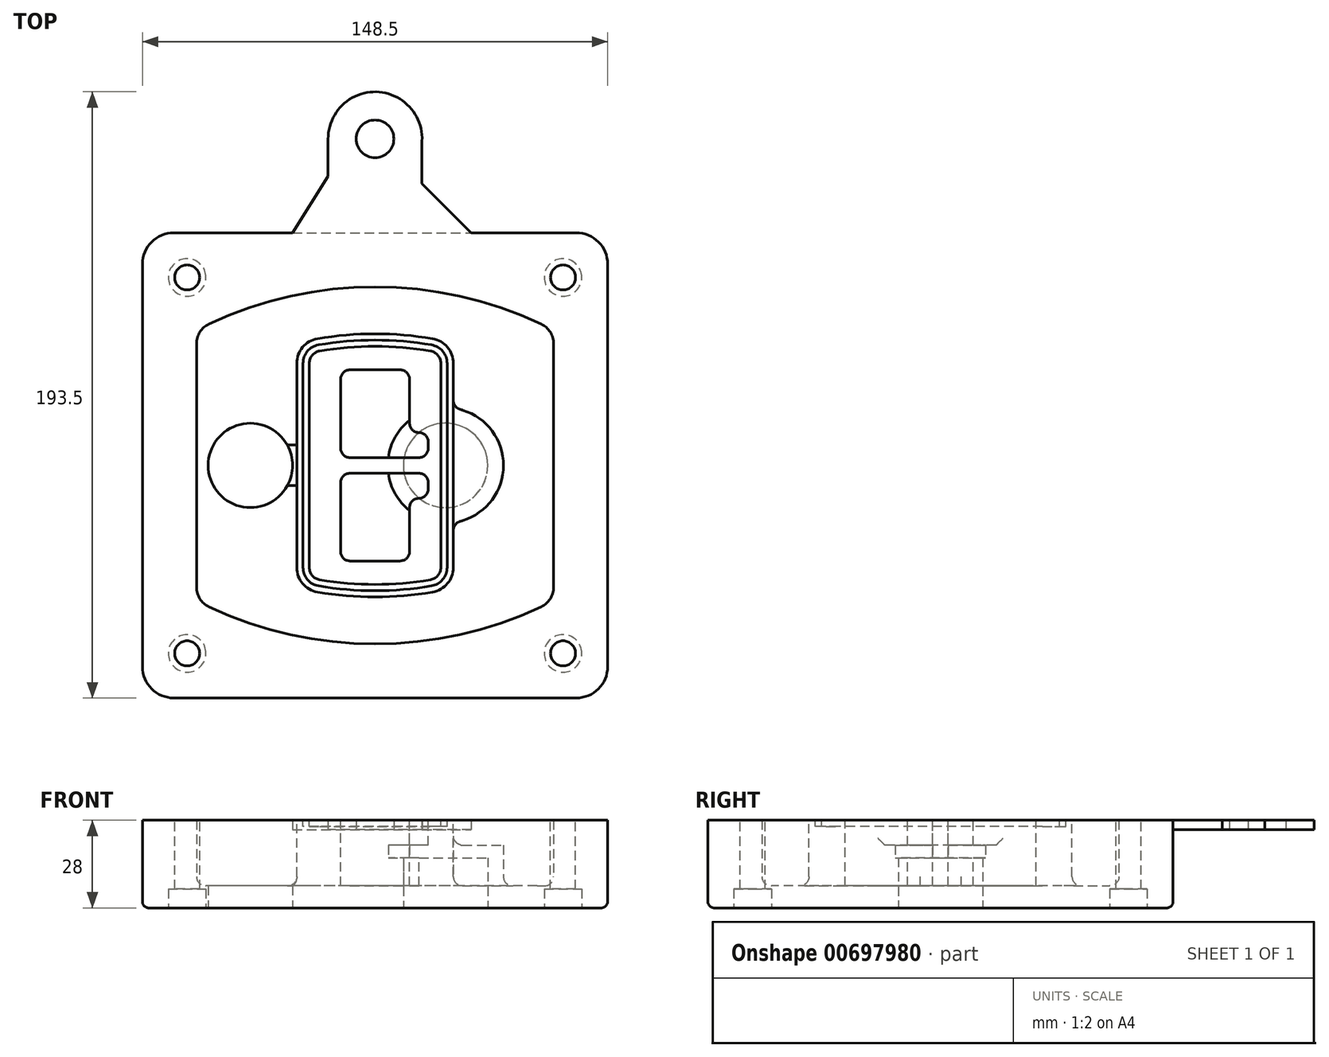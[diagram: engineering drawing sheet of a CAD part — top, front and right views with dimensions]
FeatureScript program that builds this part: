
annotation { "Feature Type Name" : "Feature", "Feature Type Description" : "" }
export const myFeature = defineFeature(function(context is Context, id is Id, definition is map)
    precondition{}
    {
        {
            var Q0;
            Q0=qCreatedBy(makeId("Top.planeOp"),FACE);
            var sketch = newSketch(context, id + "F0", { "sketchPlane" : qUnion([Q0])});
            skPoint(sketch, "E0.rect.middle", {"position": v(0, 0) * mm});
            skLineSegment(sketch, "E1.bottom", {"start": v(-64.25, -74.25) * mm, "end": v(64.25, -74.25) * mm});
            skLineSegment(sketch, "E1.top", {"start": v(-64.25, 74.25) * mm, "end": v(64.25, 74.25) * mm});
            skLineSegment(sketch, "E1.left", {"start": v(-74.25, -64.25) * mm, "end": v(-74.25, 64.25) * mm});
            skLineSegment(sketch, "E1.right", {"start": v(74.25, -64.25) * mm, "end": v(74.25, 64.25) * mm});
            skLineSegment(sketch, "E2", {"start": v(-74.25, 74.25) * mm, "end": v(74.25, -74.25) * mm, "construction": true});
            skLineSegment(sketch, "E3", {"start": v(74.25, 74.25) * mm, "end": v(-74.25, -74.25) * mm, "construction": true});
            skCircle(sketch, "E4", {"center": v(-60, 60) * mm, "radius": 4 * mm});
            skCircle(sketch, "E5", {"center": v(60, 60) * mm, "radius": 4 * mm});
            skCircle(sketch, "E6", {"center": v(60, -60) * mm, "radius": 4 * mm});
            skCircle(sketch, "E7", {"center": v(-60, -60) * mm, "radius": 4 * mm});
            skLineSegment(sketch, "E8", {"start": v(-60, 60) * mm, "end": v(60, 60) * mm, "construction": true});
            skLineSegment(sketch, "E9", {"start": v(60, 60) * mm, "end": v(60, -60) * mm, "construction": true});
            skLineSegment(sketch, "E10", {"start": v(60, -60) * mm, "end": v(-60, -60) * mm, "construction": true});
            skLineSegment(sketch, "E11", {"start": v(-60, -60) * mm, "end": v(-60, 60) * mm, "construction": true});
            skLineSegment(sketch, "E12", {"start": v(-60, 38.83) * mm, "end": v(-60, -38.83) * mm});
            skLineSegment(sketch, "E13", {"start": v(60, 38.83) * mm, "end": v(60, -38.83) * mm});
            skArc(sketch, "E14", {"start": v(54.26, 47.88) * mm, "mid": v(0, 60) * mm, "end": v(-54.26, 47.88) * mm});
            skArc(sketch, "E15", {"start": v(-54.26, -47.88) * mm, "mid": v(0, -60) * mm, "end": v(54.26, -47.88) * mm});
            skLineSegment(sketch, "E16", {"start": v(-60, 0) * mm, "end": v(60, 0) * mm, "construction": true});
            skPoint(sketch, "E17.visualSharp", {"position": v(-60, -45) * mm});
            skArc(sketch, "E17.filletArc", {"start": v(-60, -38.83) * mm, "mid": v(-58.44, -44.2) * mm, "end": v(-54.26, -47.88) * mm});
            skPoint(sketch, "E18.visualSharp", {"position": v(-60, 45) * mm});
            skArc(sketch, "E18.filletArc", {"start": v(-54.26, 47.88) * mm, "mid": v(-58.44, 44.2) * mm, "end": v(-60, 38.83) * mm});
            skPoint(sketch, "E19.visualSharp", {"position": v(60, 45) * mm});
            skArc(sketch, "E19.filletArc", {"start": v(60, 38.83) * mm, "mid": v(58.44, 44.2) * mm, "end": v(54.26, 47.88) * mm});
            skPoint(sketch, "E20.visualSharp", {"position": v(60, -45) * mm});
            skArc(sketch, "E20.filletArc", {"start": v(54.26, -47.88) * mm, "mid": v(58.44, -44.2) * mm, "end": v(60, -38.83) * mm});
            skPoint(sketch, "E21.visualSharp", {"position": v(-74.25, 74.25) * mm});
            skArc(sketch, "E21.filletArc", {"start": v(-64.25, 74.25) * mm, "mid": v(-71.32, 71.32) * mm, "end": v(-74.25, 64.25) * mm});
            skPoint(sketch, "E22.visualSharp", {"position": v(74.25, 74.25) * mm});
            skArc(sketch, "E22.filletArc", {"start": v(74.25, 64.25) * mm, "mid": v(71.32, 71.32) * mm, "end": v(64.25, 74.25) * mm});
            skPoint(sketch, "E23.visualSharp", {"position": v(74.25, -74.25) * mm});
            skArc(sketch, "E23.filletArc", {"start": v(64.25, -74.25) * mm, "mid": v(71.32, -71.32) * mm, "end": v(74.25, -64.25) * mm});
            skPoint(sketch, "E24.visualSharp", {"position": v(-74.25, -74.25) * mm});
            skArc(sketch, "E24.filletArc", {"start": v(-74.25, -64.25) * mm, "mid": v(-71.32, -71.32) * mm, "end": v(-64.25, -74.25) * mm});
            skArc(sketch, "E25.0", {"start": v(57, 38.83) * mm, "mid": v(55.9, 42.58) * mm, "end": v(52.98, 45.17) * mm});
            skLineSegment(sketch, "E25.1", {"start": v(57, 38.83) * mm, "end": v(57, -38.83) * mm});
            skArc(sketch, "E25.2", {"start": v(52.98, -45.17) * mm, "mid": v(55.9, -42.58) * mm, "end": v(57, -38.83) * mm});
            skArc(sketch, "E25.3", {"start": v(-52.98, -45.17) * mm, "mid": v(0, -57) * mm, "end": v(52.98, -45.17) * mm});
            skArc(sketch, "E25.4", {"start": v(-57, -38.83) * mm, "mid": v(-55.9, -42.58) * mm, "end": v(-52.98, -45.17) * mm});
            skArc(sketch, "E25.5", {"start": v(52.98, 45.17) * mm, "mid": v(0, 57) * mm, "end": v(-52.98, 45.17) * mm});
            skLineSegment(sketch, "E25.6", {"start": v(-57, 38.83) * mm, "end": v(-57, -38.83) * mm});
            skArc(sketch, "E25.7", {"start": v(-52.98, 45.17) * mm, "mid": v(-55.9, 42.58) * mm, "end": v(-57, 38.83) * mm});
            skArc(sketch, "E26.0", {"start": v(-55.96, 51.5) * mm, "mid": v(-61.82, 46.33) * mm, "end": v(-64, 38.83) * mm});
            skArc(sketch, "E26.1", {"start": v(55.96, 51.5) * mm, "mid": v(0, 64) * mm, "end": v(-55.96, 51.5) * mm});
            skArc(sketch, "E26.2", {"start": v(64, 38.83) * mm, "mid": v(61.82, 46.33) * mm, "end": v(55.96, 51.5) * mm});
            skLineSegment(sketch, "E26.3", {"start": v(64, 38.83) * mm, "end": v(64, -38.83) * mm});
            skArc(sketch, "E26.4", {"start": v(55.96, -51.5) * mm, "mid": v(61.82, -46.33) * mm, "end": v(64, -38.83) * mm});
            skLineSegment(sketch, "E26.5", {"start": v(-64, 38.83) * mm, "end": v(-64, -38.83) * mm});
            skArc(sketch, "E26.6", {"start": v(-55.96, -51.5) * mm, "mid": v(0, -64) * mm, "end": v(55.96, -51.5) * mm});
            skArc(sketch, "E26.7", {"start": v(-64, -38.83) * mm, "mid": v(-61.82, -46.33) * mm, "end": v(-55.96, -51.5) * mm});
            skSolve(sketch);
        }
        {
            var Q0;
            Q0=makeQuery(id+"F0.imprint","IMPRINT",FACE,{"disambiguationData":[TD([[makeQuery(id+"F0.imprint","IMPRINT",EDGE,{"derivedFrom":sQuery(id+"F0.wireOp",EDGE,"E1.bottom")}),1.0]])]});
            var Q1;
            Q1=makeQuery(id+"F0.imprint","IMPRINT",FACE,{"disambiguationData":[TD([[makeQuery(id+"F0.imprint","IMPRINT",EDGE,{"derivedFrom":sQuery(id+"F0.wireOp",EDGE,"E12")}),1.0]])]});
            var Q2;
            Q2=makeQuery(id+"F0.imprint","IMPRINT",FACE,{"disambiguationData":[TD([[makeQuery(id+"F0.imprint","IMPRINT",EDGE,{"derivedFrom":sQuery(id+"F0.wireOp",EDGE,"E25.0")}),1.0]])]});
            var Q3;
            Q3=makeQuery(id+"F0.imprint","IMPRINT",FACE,{"disambiguationData":[TD([[makeQuery(id+"F0.imprint","IMPRINT",EDGE,{"derivedFrom":sQuery(id+"F0.wireOp",EDGE,"E12")}),-1.0]])]});
            extrude(context, id + "F1", {"entities" : qUnion([Q0, Q1, Q2, Q3]), "oppositeDirection" : true, "depth" : 25 * mm});
        }
        {
            var Q0;
            Q0=makeQuery(id+"F0.imprint","IMPRINT",FACE,{"disambiguationData":[TD([[makeQuery(id+"F0.imprint","IMPRINT",EDGE,{"derivedFrom":sQuery(id+"F0.wireOp",EDGE,"E12")}),1.0]])]});
            extrude(context, id + "F2", {"entities" : qUnion([Q0]), "operationType" : NewBodyOperationType.ADD, "depth" : 3 * mm});
        }
        {
            var Q0;
            Q0=makeQuery(id+"F0.imprint","IMPRINT",FACE,{"disambiguationData":[TD([[makeQuery(id+"F0.imprint","IMPRINT",EDGE,{"derivedFrom":sQuery(id+"F0.wireOp",EDGE,"E25.0")}),1.0]])]});
            extrude(context, id + "F3", {"entities" : qUnion([Q0]), "operationType" : NewBodyOperationType.REMOVE, "oppositeDirection" : true, "depth" : 18 * mm});
        }
        {
            var Q0;
            Q0=makeQuery(id+"F2.opExtrude","CAP_FACE",FACE,{"disambiguationData":[OSD([sQuery(id+"F0.wireOp",EDGE,"E12"),sQuery(id+"F0.wireOp",EDGE,"E13"),sQuery(id+"F0.wireOp",EDGE,"E14"),sQuery(id+"F0.wireOp",EDGE,"E15"),sQuery(id+"F0.wireOp",EDGE,"E17.filletArc"),sQuery(id+"F0.wireOp",EDGE,"E18.filletArc"),sQuery(id+"F0.wireOp",EDGE,"E19.filletArc"),sQuery(id+"F0.wireOp",EDGE,"E20.filletArc"),sQuery(id+"F0.wireOp",EDGE,"E25.0"),sQuery(id+"F0.wireOp",EDGE,"E25.1"),sQuery(id+"F0.wireOp",EDGE,"E25.2"),sQuery(id+"F0.wireOp",EDGE,"E25.3"),sQuery(id+"F0.wireOp",EDGE,"E25.4"),sQuery(id+"F0.wireOp",EDGE,"E25.5"),sQuery(id+"F0.wireOp",EDGE,"E25.6"),sQuery(id+"F0.wireOp",EDGE,"E25.7")])],"isStart":false});
            var sketch = newSketch(context, id + "F4", { "sketchPlane" : qUnion([Q0])});
            skArc(sketch, "E27.0", {"start": v(-18.34, -40.45) * mm, "mid": v(0, -42) * mm, "end": v(18.34, -40.45) * mm});
            skArc(sketch, "E28.0", {"start": v(18.34, 40.45) * mm, "mid": v(0, 42) * mm, "end": v(-18.34, 40.45) * mm});
            skLineSegment(sketch, "E29", {"start": v(-25, 32.57) * mm, "end": v(-25, -32.57) * mm});
            skLineSegment(sketch, "E30", {"start": v(25, 32.57) * mm, "end": v(25, -32.57) * mm});
            skLineSegment(sketch, "E31", {"start": v(-25, 39.1) * mm, "end": v(25, 39.1) * mm, "construction": true});
            skLineSegment(sketch, "E32", {"start": v(-25, -39.1) * mm, "end": v(25, -39.1) * mm, "construction": true});
            skPoint(sketch, "E33.visualSharp", {"position": v(-25, 39.1) * mm});
            skArc(sketch, "E33.filletArc", {"start": v(-18.34, 40.45) * mm, "mid": v(-23.11, 37.73) * mm, "end": v(-25, 32.57) * mm});
            skPoint(sketch, "E34.visualSharp", {"position": v(25, 39.1) * mm});
            skArc(sketch, "E34.filletArc", {"start": v(25, 32.57) * mm, "mid": v(23.11, 37.73) * mm, "end": v(18.34, 40.45) * mm});
            skPoint(sketch, "E35.visualSharp", {"position": v(25, -39.1) * mm});
            skArc(sketch, "E35.filletArc", {"start": v(18.34, -40.45) * mm, "mid": v(23.11, -37.73) * mm, "end": v(25, -32.57) * mm});
            skPoint(sketch, "E36.visualSharp", {"position": v(-25, -39.1) * mm});
            skArc(sketch, "E36.filletArc", {"start": v(-25, -32.57) * mm, "mid": v(-23.11, -37.73) * mm, "end": v(-18.34, -40.45) * mm});
            skArc(sketch, "E37.0", {"start": v(52.98, 45.17) * mm, "mid": v(0, 57) * mm, "end": v(-52.98, 45.17) * mm});
            skArc(sketch, "E37.1", {"start": v(-52.98, 45.17) * mm, "mid": v(-55.9, 42.58) * mm, "end": v(-57, 38.83) * mm});
            skLineSegment(sketch, "E37.2", {"start": v(-57, 38.83) * mm, "end": v(-57, -38.83) * mm});
            skArc(sketch, "E37.3", {"start": v(-57, -38.83) * mm, "mid": v(-55.9, -42.58) * mm, "end": v(-52.98, -45.17) * mm});
            skArc(sketch, "E37.4", {"start": v(-52.98, -45.17) * mm, "mid": v(0, -57) * mm, "end": v(52.98, -45.17) * mm});
            skArc(sketch, "E37.5", {"start": v(52.98, -45.17) * mm, "mid": v(55.9, -42.58) * mm, "end": v(57, -38.83) * mm});
            skLineSegment(sketch, "E37.6", {"start": v(57, 38.83) * mm, "end": v(57, -38.83) * mm});
            skArc(sketch, "E37.7", {"start": v(57, 38.83) * mm, "mid": v(55.9, 42.58) * mm, "end": v(52.98, 45.17) * mm});
            skLineSegment(sketch, "E38.0", {"start": v(23, 32.57) * mm, "end": v(23, -32.57) * mm});
            skArc(sketch, "E38.1", {"start": v(18, -38.48) * mm, "mid": v(21.58, -36.44) * mm, "end": v(23, -32.57) * mm});
            skArc(sketch, "E38.2", {"start": v(-18, -38.48) * mm, "mid": v(0, -40) * mm, "end": v(18, -38.48) * mm});
            skArc(sketch, "E38.3", {"start": v(-23, -32.57) * mm, "mid": v(-21.58, -36.44) * mm, "end": v(-18, -38.48) * mm});
            skLineSegment(sketch, "E38.4", {"start": v(-23, 32.57) * mm, "end": v(-23, -32.57) * mm});
            skArc(sketch, "E38.5", {"start": v(23, 32.57) * mm, "mid": v(21.58, 36.44) * mm, "end": v(18, 38.48) * mm});
            skArc(sketch, "E38.6", {"start": v(-18, 38.48) * mm, "mid": v(-21.58, 36.44) * mm, "end": v(-23, 32.57) * mm});
            skArc(sketch, "E38.7", {"start": v(18, 38.48) * mm, "mid": v(0, 40) * mm, "end": v(-18, 38.48) * mm});
            skArc(sketch, "E39.0", {"start": v(21, 32.57) * mm, "mid": v(20.06, 35.15) * mm, "end": v(17.67, 36.5) * mm});
            skLineSegment(sketch, "E39.1", {"start": v(21, 32.57) * mm, "end": v(21, -32.57) * mm});
            skArc(sketch, "E39.2", {"start": v(17.67, -36.5) * mm, "mid": v(20.06, -35.15) * mm, "end": v(21, -32.57) * mm});
            skArc(sketch, "E39.3", {"start": v(-17.67, -36.5) * mm, "mid": v(0, -38) * mm, "end": v(17.67, -36.5) * mm});
            skArc(sketch, "E39.4", {"start": v(-21, -32.57) * mm, "mid": v(-20.06, -35.15) * mm, "end": v(-17.67, -36.5) * mm});
            skArc(sketch, "E39.5", {"start": v(17.67, 36.5) * mm, "mid": v(0, 38) * mm, "end": v(-17.67, 36.5) * mm});
            skLineSegment(sketch, "E39.6", {"start": v(-21, 32.57) * mm, "end": v(-21, -32.57) * mm});
            skArc(sketch, "E39.7", {"start": v(-17.67, 36.5) * mm, "mid": v(-20.06, 35.15) * mm, "end": v(-21, 32.57) * mm});
            skLineSegment(sketch, "E40", {"start": v(-25, 0) * mm, "end": v(25, 0) * mm, "construction": true});
            skLineSegment(sketch, "E41", {"start": v(-11, 5.5) * mm, "end": v(-11, 27.5) * mm});
            skLineSegment(sketch, "E42", {"start": v(-8, 30.5) * mm, "end": v(8, 30.5) * mm});
            skLineSegment(sketch, "E43", {"start": v(11, 27.5) * mm, "end": v(11, 13.5) * mm});
            skLineSegment(sketch, "E44", {"start": v(14, 10.5) * mm, "end": v(14, 10.5) * mm});
            skLineSegment(sketch, "E45", {"start": v(17, 7.5) * mm, "end": v(17, 5.5) * mm});
            skLineSegment(sketch, "E46", {"start": v(14, 2.5) * mm, "end": v(-8, 2.5) * mm});
            skPoint(sketch, "E47.visualSharp", {"position": v(-11, 30.5) * mm});
            skArc(sketch, "E47.filletArc", {"start": v(-8, 30.5) * mm, "mid": v(-10.12, 29.62) * mm, "end": v(-11, 27.5) * mm});
            skPoint(sketch, "E48.visualSharp", {"position": v(11, 30.5) * mm});
            skArc(sketch, "E48.filletArc", {"start": v(11, 27.5) * mm, "mid": v(10.12, 29.62) * mm, "end": v(8, 30.5) * mm});
            skPoint(sketch, "E49.visualSharp", {"position": v(11, 10.5) * mm});
            skArc(sketch, "E49.filletArc", {"start": v(11, 13.5) * mm, "mid": v(11.88, 11.38) * mm, "end": v(14, 10.5) * mm});
            skPoint(sketch, "E50.visualSharp", {"position": v(17, 10.5) * mm});
            skArc(sketch, "E50.filletArc", {"start": v(17, 7.5) * mm, "mid": v(16.12, 9.62) * mm, "end": v(14, 10.5) * mm});
            skPoint(sketch, "E51.visualSharp", {"position": v(17, 2.5) * mm});
            skArc(sketch, "E51.filletArc", {"start": v(14, 2.5) * mm, "mid": v(16.12, 3.38) * mm, "end": v(17, 5.5) * mm});
            skPoint(sketch, "E52.visualSharp", {"position": v(-11, 2.5) * mm});
            skArc(sketch, "E52.filletArc", {"start": v(-11, 5.5) * mm, "mid": v(-10.12, 3.38) * mm, "end": v(-8, 2.5) * mm});
            skLineSegment(sketch, "E53.0.MirrorCS", {"start": v(14, -2.5) * mm, "end": v(-8, -2.5) * mm});
            skArc(sketch, "E54.0.MirrorCS", {"start": v(-11, -5.5) * mm, "mid": v(-10.12, -3.38) * mm, "end": v(-8, -2.5) * mm});
            skLineSegment(sketch, "E55.0.MirrorCS", {"start": v(-11, -5.5) * mm, "end": v(-11, -27.5) * mm});
            skArc(sketch, "E56.0.MirrorCS", {"start": v(-8, -30.5) * mm, "mid": v(-10.12, -29.62) * mm, "end": v(-11, -27.5) * mm});
            skLineSegment(sketch, "E57.0.MirrorCS", {"start": v(-8, -30.5) * mm, "end": v(8, -30.5) * mm});
            skArc(sketch, "E58.0.MirrorCS", {"start": v(11, -27.5) * mm, "mid": v(10.12, -29.62) * mm, "end": v(8, -30.5) * mm});
            skLineSegment(sketch, "E59.0.MirrorCS", {"start": v(11, -27.5) * mm, "end": v(11, -13.5) * mm});
            skArc(sketch, "E60.0.MirrorCS", {"start": v(11, -13.5) * mm, "mid": v(11.88, -11.38) * mm, "end": v(14, -10.5) * mm});
            skArc(sketch, "E61.0.MirrorCS", {"start": v(17, -7.5) * mm, "mid": v(16.12, -9.62) * mm, "end": v(14, -10.5) * mm});
            skLineSegment(sketch, "E62.0.MirrorCS", {"start": v(17, -7.5) * mm, "end": v(17, -5.5) * mm});
            skArc(sketch, "E63.0.MirrorCS", {"start": v(14, -2.5) * mm, "mid": v(16.12, -3.38) * mm, "end": v(17, -5.5) * mm});
            skSolve(sketch);
        }
        {
            var Q0;
            Q0=makeQuery(id+"F4.imprint","IMPRINT",FACE,{"disambiguationData":[TD([[makeQuery(id+"F4.imprint","IMPRINT",EDGE,{"derivedFrom":sQuery(id+"F4.wireOp",EDGE,"E27.0")}),1.0]])]});
            var Q1;
            Q1=makeQuery(id+"F4.imprint","IMPRINT",FACE,{"disambiguationData":[TD([[makeQuery(id+"F4.imprint","IMPRINT",EDGE,{"derivedFrom":sQuery(id+"F4.wireOp",EDGE,"E38.0")}),-1.0]])]});
            var Q2;
            Q2=makeQuery(id+"F4.imprint","IMPRINT",FACE,{"disambiguationData":[TD([[makeQuery(id+"F4.imprint","IMPRINT",EDGE,{"derivedFrom":sQuery(id+"F4.wireOp",EDGE,"E39.0")}),1.0]])]});
            extrude(context, id + "F5", {"entities" : qUnion([Q0, Q1, Q2]), "operationType" : NewBodyOperationType.ADD, "endBound" : BoundingType.UP_TO_NEXT, "oppositeDirection" : true, "depth" : 25 * mm});
        }
        {
            var Q0;
            Q0=makeQuery(id+"F4.imprint","IMPRINT",FACE,{"disambiguationData":[TD([[makeQuery(id+"F4.imprint","IMPRINT",EDGE,{"derivedFrom":sQuery(id+"F4.wireOp",EDGE,"E38.0")}),-1.0]])]});
            extrude(context, id + "F6", {"entities" : qUnion([Q0]), "operationType" : NewBodyOperationType.REMOVE, "oppositeDirection" : true, "depth" : 2 * mm});
        }
        {
            var Q0;
            Q0=makeQuery(id+"F1.opExtrude","CAP_FACE",FACE,{"disambiguationData":[OSD([sQuery(id+"F0.wireOp",EDGE,"E1.bottom"),sQuery(id+"F0.wireOp",EDGE,"E1.top"),sQuery(id+"F0.wireOp",EDGE,"E1.left"),sQuery(id+"F0.wireOp",EDGE,"E1.right"),sQuery(id+"F0.wireOp",EDGE,"E4"),sQuery(id+"F0.wireOp",EDGE,"E5"),sQuery(id+"F0.wireOp",EDGE,"E6"),sQuery(id+"F0.wireOp",EDGE,"E7"),sQuery(id+"F0.wireOp",EDGE,"E21.filletArc"),sQuery(id+"F0.wireOp",EDGE,"E22.filletArc"),sQuery(id+"F0.wireOp",EDGE,"E23.filletArc"),sQuery(id+"F0.wireOp",EDGE,"E24.filletArc")])],"isStart":false});
            var sketch = newSketch(context, id + "F7", { "sketchPlane" : qUnion([Q0])});
            skCircle(sketch, "E64", {"center": v(22.5, 0) * mm, "radius": 13.47 * mm});
            skCircle(sketch, "E65", {"center": v(-39.81, 0) * mm, "radius": 13.47 * mm});
            skLineSegment(sketch, "E66", {"start": v(74.25, 0) * mm, "end": v(-74.25, 0) * mm});
            skCircle(sketch, "E67", {"center": v(22.5, 0) * mm, "radius": 18.47 * mm});
            skCircle(sketch, "E68", {"center": v(60, -60) * mm, "radius": 6 * mm});
            skCircle(sketch, "E69", {"center": v(-60, -60) * mm, "radius": 6 * mm});
            skCircle(sketch, "E70", {"center": v(-60, 60) * mm, "radius": 6 * mm});
            skCircle(sketch, "E71", {"center": v(60, 60) * mm, "radius": 6 * mm});
            skSolve(sketch);
        }
        {
            var Q0;
            {var subQ1=sQuery(id+"F7.wireOp",EDGE,"E66");var subQ4=sQuery(id+"F7.wireOp",EDGE,"E64");var subQ6=makeQuery(id+"F7.imprint","INTERSECT",VERTEX,{"disambiguationData":[OD(0.0)],"derivedFrom":[subQ4,subQ1]});Q0=makeQuery(id+"F7.imprint","IMPRINT",FACE,{"disambiguationData":[TD([[makeQuery(id+"F7.imprint","IMPRINT",EDGE,{"disambiguationData":[TD([[subQ6,-1.0]])],"derivedFrom":subQ4}),-1.0]])]});}
            var Q1;
            {var subQ0=sQuery(id+"F7.wireOp",EDGE,"E66");var subQ1=sQuery(id+"F7.wireOp",EDGE,"E64");var subQ3=makeQuery(id+"F7.imprint","INTERSECT",VERTEX,{"disambiguationData":[OD(0.0)],"derivedFrom":[subQ1,subQ0]});Q1=makeQuery(id+"F7.imprint","IMPRINT",FACE,{"disambiguationData":[TD([[makeQuery(id+"F7.imprint","IMPRINT",EDGE,{"disambiguationData":[TD([[subQ3,-1.0]])],"derivedFrom":subQ1}),1.0]])]});}
            var Q2;
            {var subQ0=sQuery(id+"F7.wireOp",EDGE,"E66");var subQ1=sQuery(id+"F7.wireOp",EDGE,"E64");var subQ3=makeQuery(id+"F7.imprint","INTERSECT",VERTEX,{"disambiguationData":[OD(0.0)],"derivedFrom":[subQ1,subQ0]});Q2=makeQuery(id+"F7.imprint","IMPRINT",FACE,{"disambiguationData":[TD([[makeQuery(id+"F7.imprint","IMPRINT",EDGE,{"disambiguationData":[TD([[subQ3,1.0]])],"derivedFrom":subQ1}),1.0]])]});}
            var Q3;
            {var subQ1=sQuery(id+"F7.wireOp",EDGE,"E66");var subQ4=sQuery(id+"F7.wireOp",EDGE,"E64");var subQ6=makeQuery(id+"F7.imprint","INTERSECT",VERTEX,{"disambiguationData":[OD(0.0)],"derivedFrom":[subQ4,subQ1]});Q3=makeQuery(id+"F7.imprint","IMPRINT",FACE,{"disambiguationData":[TD([[makeQuery(id+"F7.imprint","IMPRINT",EDGE,{"disambiguationData":[TD([[subQ6,1.0]])],"derivedFrom":subQ4}),-1.0]])]});}
            extrude(context, id + "F8", {"entities" : qUnion([Q0, Q1, Q2, Q3]), "operationType" : NewBodyOperationType.ADD, "oppositeDirection" : true, "depth" : 20 * mm});
        }
        {
            var Q0;
            {var subQ0=sQuery(id+"F7.wireOp",EDGE,"E66");var subQ1=sQuery(id+"F7.wireOp",EDGE,"E64");var subQ3=makeQuery(id+"F7.imprint","INTERSECT",VERTEX,{"disambiguationData":[OD(0.0)],"derivedFrom":[subQ1,subQ0]});Q0=makeQuery(id+"F7.imprint","IMPRINT",FACE,{"disambiguationData":[TD([[makeQuery(id+"F7.imprint","IMPRINT",EDGE,{"disambiguationData":[TD([[subQ3,-1.0]])],"derivedFrom":subQ1}),1.0]])]});}
            var Q1;
            {var subQ0=sQuery(id+"F7.wireOp",EDGE,"E66");var subQ1=sQuery(id+"F7.wireOp",EDGE,"E64");var subQ3=makeQuery(id+"F7.imprint","INTERSECT",VERTEX,{"disambiguationData":[OD(0.0)],"derivedFrom":[subQ1,subQ0]});Q1=makeQuery(id+"F7.imprint","IMPRINT",FACE,{"disambiguationData":[TD([[makeQuery(id+"F7.imprint","IMPRINT",EDGE,{"disambiguationData":[TD([[subQ3,1.0]])],"derivedFrom":subQ1}),1.0]])]});}
            extrude(context, id + "F9", {"entities" : qUnion([Q0, Q1]), "operationType" : NewBodyOperationType.REMOVE, "oppositeDirection" : true, "depth" : 16 * mm});
        }
        {
            var Q0;
            {var subQ0=sQuery(id+"F7.wireOp",EDGE,"E66");var subQ1=sQuery(id+"F7.wireOp",EDGE,"E65");var subQ3=makeQuery(id+"F7.imprint","INTERSECT",VERTEX,{"disambiguationData":[OD(0.0)],"derivedFrom":[subQ1,subQ0]});Q0=makeQuery(id+"F7.imprint","IMPRINT",FACE,{"disambiguationData":[TD([[makeQuery(id+"F7.imprint","IMPRINT",EDGE,{"disambiguationData":[TD([[subQ3,-1.0]])],"derivedFrom":subQ1}),1.0]])]});}
            var Q1;
            {var subQ0=sQuery(id+"F7.wireOp",EDGE,"E66");var subQ1=sQuery(id+"F7.wireOp",EDGE,"E65");var subQ3=makeQuery(id+"F7.imprint","INTERSECT",VERTEX,{"disambiguationData":[OD(0.0)],"derivedFrom":[subQ1,subQ0]});Q1=makeQuery(id+"F7.imprint","IMPRINT",FACE,{"disambiguationData":[TD([[makeQuery(id+"F7.imprint","IMPRINT",EDGE,{"disambiguationData":[TD([[subQ3,1.0]])],"derivedFrom":subQ1}),1.0]])]});}
            extrude(context, id + "F10", {"entities" : qUnion([Q0, Q1]), "operationType" : NewBodyOperationType.REMOVE, "oppositeDirection" : true, "depth" : 25 * mm});
        }
        {
            var Q0;
            Q0=makeQuery(id+"F7.imprint","IMPRINT",FACE,{"disambiguationData":[TD([[makeQuery(id+"F7.imprint","IMPRINT",EDGE,{"derivedFrom":sQuery(id+"F7.wireOp",EDGE,"E68")}),1.0]])]});
            var Q1;
            Q1=makeQuery(id+"F7.imprint","IMPRINT",FACE,{"disambiguationData":[TD([[makeQuery(id+"F7.imprint","IMPRINT",EDGE,{"derivedFrom":makeQuery(id+"F1.opExtrude","CAP_EDGE",EDGE,{"disambiguationData":[OSD([sQuery(id+"F0.wireOp",EDGE,"E5")])],"isStart":false})}),-1.0]])]});
            var Q2;
            Q2=makeQuery(id+"F7.imprint","IMPRINT",FACE,{"disambiguationData":[TD([[makeQuery(id+"F7.imprint","IMPRINT",EDGE,{"derivedFrom":sQuery(id+"F7.wireOp",EDGE,"E69")}),1.0]])]});
            var Q3;
            Q3=makeQuery(id+"F7.imprint","IMPRINT",FACE,{"disambiguationData":[TD([[makeQuery(id+"F7.imprint","IMPRINT",EDGE,{"derivedFrom":makeQuery(id+"F1.opExtrude","CAP_EDGE",EDGE,{"disambiguationData":[OSD([sQuery(id+"F0.wireOp",EDGE,"E4")])],"isStart":false})}),-1.0]])]});
            var Q4;
            Q4=makeQuery(id+"F7.imprint","IMPRINT",FACE,{"disambiguationData":[TD([[makeQuery(id+"F7.imprint","IMPRINT",EDGE,{"derivedFrom":sQuery(id+"F7.wireOp",EDGE,"E70")}),1.0]])]});
            var Q5;
            Q5=makeQuery(id+"F7.imprint","IMPRINT",FACE,{"disambiguationData":[TD([[makeQuery(id+"F7.imprint","IMPRINT",EDGE,{"derivedFrom":makeQuery(id+"F1.opExtrude","CAP_EDGE",EDGE,{"disambiguationData":[OSD([sQuery(id+"F0.wireOp",EDGE,"E7")])],"isStart":false})}),-1.0]])]});
            var Q6;
            Q6=makeQuery(id+"F7.imprint","IMPRINT",FACE,{"disambiguationData":[TD([[makeQuery(id+"F7.imprint","IMPRINT",EDGE,{"derivedFrom":sQuery(id+"F7.wireOp",EDGE,"E71")}),1.0]])]});
            var Q7;
            Q7=makeQuery(id+"F7.imprint","IMPRINT",FACE,{"disambiguationData":[TD([[makeQuery(id+"F7.imprint","IMPRINT",EDGE,{"derivedFrom":makeQuery(id+"F1.opExtrude","CAP_EDGE",EDGE,{"disambiguationData":[OSD([sQuery(id+"F0.wireOp",EDGE,"E6")])],"isStart":false})}),-1.0]])]});
            extrude(context, id + "F11", {"entities" : qUnion([Q0, Q1, Q2, Q3, Q4, Q5, Q6, Q7]), "operationType" : NewBodyOperationType.REMOVE, "oppositeDirection" : true, "depth" : 6 * mm});
        }
        {
            var Q0;
            Q0=makeQuery(id+"F9.boolean.opBoolean","COPY",FACE,{"derivedFrom":makeQuery(id+"F9.opExtrude","CAP_FACE",FACE,{"disambiguationData":[OSD([sQuery(id+"F7.wireOp",EDGE,"E64")])],"isStart":false})});
            var sketch = newSketch(context, id + "F12", { "sketchPlane" : qUnion([Q0])});
            skArc(sketch, "E72.0", {"start": v(11, 14.45) * mm, "mid": v(6.45, 9.13) * mm, "end": v(4.2, 2.5) * mm});
            skArc(sketch, "E72.1", {"start": v(4.2, -2.5) * mm, "mid": v(6.45, -9.13) * mm, "end": v(11, -14.45) * mm});
            skLineSegment(sketch, "E73", {"start": v(4.2, -2.5) * mm, "end": v(14, -2.5) * mm});
            skLineSegment(sketch, "E74.0", {"start": v(14, 2.5) * mm, "end": v(4.2, 2.5) * mm});
            skArc(sketch, "E74.1", {"start": v(14, 2.5) * mm, "mid": v(16.12, 3.38) * mm, "end": v(17, 5.5) * mm});
            skLineSegment(sketch, "E74.2", {"start": v(17, 7.5) * mm, "end": v(17, 5.5) * mm});
            skArc(sketch, "E74.3", {"start": v(17, 7.5) * mm, "mid": v(16.12, 9.62) * mm, "end": v(14, 10.5) * mm});
            skArc(sketch, "E74.4", {"start": v(11, 13.5) * mm, "mid": v(11.88, 11.38) * mm, "end": v(14, 10.5) * mm});
            skLineSegment(sketch, "E74.5", {"start": v(11, 14.45) * mm, "end": v(11, 13.5) * mm});
            skLineSegment(sketch, "E74.7", {"start": v(14, -2.5) * mm, "end": v(4.2, -2.5) * mm});
            skArc(sketch, "E74.8", {"start": v(14, -2.5) * mm, "mid": v(16.12, -3.38) * mm, "end": v(17, -5.5) * mm});
            skLineSegment(sketch, "E74.9", {"start": v(17, -7.5) * mm, "end": v(17, -5.5) * mm});
            skArc(sketch, "E74.10", {"start": v(17, -7.5) * mm, "mid": v(16.12, -9.62) * mm, "end": v(14, -10.5) * mm});
            skArc(sketch, "E74.11", {"start": v(11, -13.5) * mm, "mid": v(11.88, -11.38) * mm, "end": v(14, -10.5) * mm});
            skLineSegment(sketch, "E74.12", {"start": v(11, -14.45) * mm, "end": v(11, -13.5) * mm});
            skPoint(sketch, "E75.orphan", {"position": v(11, -27.5) * mm});
            skPoint(sketch, "E76.orphan", {"position": v(-8, -2.5) * mm});
            skPoint(sketch, "E77.orphan", {"position": v(-8, 2.5) * mm});
            skPoint(sketch, "E78.orphan", {"position": v(11, 27.5) * mm});
            skSolve(sketch);
        }
        {
            var Q0;
            {var subQ7=sQuery(id+"F12.wireOp",EDGE,"E72.0");var subQ14=sQuery(id+"F12.wireOp",EDGE,"E72.1");var subQ16=sQuery(id+"F12.wireOp",EDGE,"E74.1");var subQ18=sQuery(id+"F12.wireOp",EDGE,"E74.8");Q0=qUnion([makeQuery(id+"F12.imprint","IMPRINT",FACE,{"disambiguationData":[TD([[makeQuery(id+"F12.imprint","IMPRINT",EDGE,{"derivedFrom":subQ7}),1.0]])]}),makeQuery(id+"F12.imprint","IMPRINT",FACE,{"disambiguationData":[TD([[makeQuery(id+"F12.imprint","IMPRINT",EDGE,{"derivedFrom":subQ14}),1.0]])]}),makeQuery(id+"F12.imprint","IMPRINT",FACE,{"disambiguationData":[TD([[makeQuery(id+"F12.imprint","IMPRINT",EDGE,{"derivedFrom":subQ16}),1.0]])]}),makeQuery(id+"F12.imprint","IMPRINT",FACE,{"disambiguationData":[TD([[makeQuery(id+"F12.imprint","IMPRINT",EDGE,{"derivedFrom":subQ18}),-1.0]])]})]);}
            var Q1;
            Q1=makeQuery(id+"F5.boolean.opBoolean","SPLIT",FACE,{"disambiguationData":[TD([makeQuery(id+"F5.opExtrude","SWEPT_FACE",FACE,{"disambiguationData":[OSD([sQuery(id+"F4.wireOp",EDGE,"E41")])]})])],"derivedFrom":makeQuery(id+"F3.boolean.opBoolean","COPY",FACE,{"derivedFrom":makeQuery(id+"F3.opExtrude","CAP_FACE",FACE,{"disambiguationData":[OSD([sQuery(id+"F0.wireOp",EDGE,"E25.0"),sQuery(id+"F0.wireOp",EDGE,"E25.1"),sQuery(id+"F0.wireOp",EDGE,"E25.2"),sQuery(id+"F0.wireOp",EDGE,"E25.3"),sQuery(id+"F0.wireOp",EDGE,"E25.4"),sQuery(id+"F0.wireOp",EDGE,"E25.5"),sQuery(id+"F0.wireOp",EDGE,"E25.6"),sQuery(id+"F0.wireOp",EDGE,"E25.7")])],"isStart":false})})});
            extrude(context, id + "F13", {"entities" : qUnion([Q0]), "operationType" : NewBodyOperationType.REMOVE, "endBound" : BoundingType.UP_TO_SURFACE, "endBoundEntityFace" : qUnion([Q1]), "depth" : 25 * mm});
        }
        {
            var Q0;
            Q0=makeQuery(id+"F3.boolean.opBoolean","COPY",EDGE,{"derivedFrom":makeQuery(id+"F3.opExtrude","CAP_EDGE",EDGE,{"disambiguationData":[OSD([sQuery(id+"F0.wireOp",EDGE,"E25.6")])],"isStart":false})});
            var Q1;
            Q1=makeQuery(id+"F8.boolean.opBoolean","INTERSECT",EDGE,{"derivedFrom":[makeQuery(id+"F5.opExtrude","SWEPT_FACE",FACE,{"disambiguationData":[OSD([sQuery(id+"F4.wireOp",EDGE,"E30")])]}),makeQuery(id+"F8.opExtrude","CAP_FACE",FACE,{"disambiguationData":[OSD([sQuery(id+"F7.wireOp",EDGE,"E67")])],"isStart":false})]});
            var Q2;
            Q2=makeQuery(id+"F8.boolean.opBoolean","INTERSECT",EDGE,{"disambiguationData":[OD(1.0)],"derivedFrom":[makeQuery(id+"F5.opExtrude","SWEPT_FACE",FACE,{"disambiguationData":[OSD([sQuery(id+"F4.wireOp",EDGE,"E30")])]}),makeQuery(id+"F8.opExtrude","SWEPT_FACE",FACE,{"disambiguationData":[OSD([sQuery(id+"F7.wireOp",EDGE,"E67")])]})]});
            var Q3;
            {var subQ0=sQuery(id+"F4.wireOp",EDGE,"E30");Q3=makeQuery(id+"F8.boolean.opBoolean","SPLIT",EDGE,{"disambiguationData":[TD([makeQuery(id+"F5.opExtrude","SWEPT_FACE",FACE,{"disambiguationData":[OSD([sQuery(id+"F4.wireOp",EDGE,"E35.filletArc")])]})])],"derivedFrom":makeQuery(id+"F5.opExtrude","CAP_EDGE",EDGE,{"disambiguationData":[OSD([subQ0])],"isStart":false})});}
            var Q4;
            {var subQ0=sQuery(id+"F0.wireOp",EDGE,"E25.7");var subQ1=sQuery(id+"F0.wireOp",EDGE,"E25.1");var subQ2=sQuery(id+"F0.wireOp",EDGE,"E25.6");var subQ3=sQuery(id+"F0.wireOp",EDGE,"E25.5");var subQ4=sQuery(id+"F0.wireOp",EDGE,"E25.4");var subQ5=sQuery(id+"F0.wireOp",EDGE,"E25.0");var subQ6=sQuery(id+"F0.wireOp",EDGE,"E25.2");var subQ7=sQuery(id+"F0.wireOp",EDGE,"E25.3");Q4=makeQuery(id+"F8.boolean.opBoolean","INTERSECT",EDGE,{"derivedFrom":[makeQuery(id+"F5.boolean.opBoolean","SPLIT",FACE,{"disambiguationData":[TD([makeQuery(id+"F2.opExtrude","SWEPT_FACE",FACE,{"disambiguationData":[OSD([subQ5])]})])],"derivedFrom":makeQuery(id+"F3.boolean.opBoolean","COPY",FACE,{"derivedFrom":makeQuery(id+"F3.opExtrude","CAP_FACE",FACE,{"disambiguationData":[OSD([subQ5,subQ1,subQ6,subQ7,subQ4,subQ3,subQ2,subQ0])],"isStart":false})})}),makeQuery(id+"F8.opExtrude","SWEPT_FACE",FACE,{"disambiguationData":[OSD([sQuery(id+"F7.wireOp",EDGE,"E67")])]})]});}
            var Q5;
            Q5=makeQuery(id+"F8.boolean.opBoolean","INTERSECT",EDGE,{"disambiguationData":[OD(0.0)],"derivedFrom":[makeQuery(id+"F5.opExtrude","SWEPT_FACE",FACE,{"disambiguationData":[OSD([sQuery(id+"F4.wireOp",EDGE,"E30")])]}),makeQuery(id+"F8.opExtrude","SWEPT_FACE",FACE,{"disambiguationData":[OSD([sQuery(id+"F7.wireOp",EDGE,"E67")])]})]});
            fillet(context, id + "F14", {"entities" : qUnion([Q0, Q1, Q2, Q3, Q4, Q5]), "radius" : 3 * mm, "tangentPropagation" : true, "allowEdgeOverflow" : false});
        }
        {
            var Q0;
            Q0=makeQuery(id+"F1.opExtrude","CAP_EDGE",EDGE,{"disambiguationData":[OSD([sQuery(id+"F0.wireOp",EDGE,"E1.bottom")])],"isStart":false});
            fillet(context, id + "F15", {"entities" : qUnion([Q0]), "radius" : 2 * mm, "tangentPropagation" : true, "allowEdgeOverflow" : false});
        }
        {
            var Q0;
            {var subQ0=sQuery(id+"F0.wireOp",EDGE,"E21.filletArc");var subQ1=sQuery(id+"F0.wireOp",EDGE,"E7");var subQ2=sQuery(id+"F0.wireOp",EDGE,"E6");var subQ3=sQuery(id+"F0.wireOp",EDGE,"E5");var subQ4=sQuery(id+"F0.wireOp",EDGE,"E4");var subQ5=sQuery(id+"F0.wireOp",EDGE,"E22.filletArc");var subQ6=sQuery(id+"F0.wireOp",EDGE,"E1.bottom");var subQ7=sQuery(id+"F0.wireOp",EDGE,"E1.right");var subQ8=sQuery(id+"F0.wireOp",EDGE,"E1.top");var subQ9=sQuery(id+"F0.wireOp",EDGE,"E1.left");var subQ10=sQuery(id+"F0.wireOp",EDGE,"E23.filletArc");var subQ11=sQuery(id+"F0.wireOp",EDGE,"E24.filletArc");Q0=makeQuery(id+"F2.boolean.opBoolean","SPLIT",FACE,{"disambiguationData":[TD([makeQuery(id+"F1.opExtrude","SWEPT_FACE",FACE,{"disambiguationData":[OSD([subQ6])]})])],"derivedFrom":makeQuery(id+"F1.opExtrude","CAP_FACE",FACE,{"disambiguationData":[OSD([subQ6,subQ8,subQ9,subQ7,subQ4,subQ3,subQ2,subQ1,subQ0,subQ5,subQ10,subQ11])],"isStart":true})});}
            var sketch = newSketch(context, id + "F16", { "sketchPlane" : qUnion([Q0])});
            skLineSegment(sketch, "E79", {"start": v(0, 74.25) * mm, "end": v(0, 104.25) * mm, "construction": true});
            skPoint(sketch, "E79.endSnap0", {"position": v(0, 74.25) * mm});
            skCircle(sketch, "E80", {"center": v(0, 104.25) * mm, "radius": 6 * mm});
            skLineSegment(sketch, "E81", {"start": v(-26.34, 74.25) * mm, "end": v(-15, 92.25) * mm});
            skLineSegment(sketch, "E82", {"start": v(30.7, 74.25) * mm, "end": v(14.98, 89.96) * mm});
            skLineSegment(sketch, "E83", {"start": v(14.98, 89.96) * mm, "end": v(14.98, 103.58) * mm});
            skLineSegment(sketch, "E84", {"start": v(-15, 92.25) * mm, "end": v(-15, 104.25) * mm});
            skArc(sketch, "E85", {"start": v(14.98, 103.58) * mm, "mid": v(0.34, 119.25) * mm, "end": v(-15, 104.25) * mm});
            skLineSegment(sketch, "E86", {"start": v(-74.25, 0) * mm, "end": v(74.25, 0) * mm, "construction": true});
            skArc(sketch, "E87.MirrorCS", {"start": v(14.98, -103.58) * mm, "mid": v(0.34, -119.25) * mm, "end": v(-15, -104.25) * mm});
            skLineSegment(sketch, "E88.MirrorCS", {"start": v(14.98, -89.96) * mm, "end": v(14.98, -103.58) * mm});
            skLineSegment(sketch, "E89.MirrorCS", {"start": v(30.7, -74.25) * mm, "end": v(14.98, -89.96) * mm});
            skCircle(sketch, "E90.MirrorC", {"center": v(0, -104.25) * mm, "radius": 6 * mm});
            skLineSegment(sketch, "E91.MirrorCS", {"start": v(-15, -92.25) * mm, "end": v(-15, -104.25) * mm});
            skLineSegment(sketch, "E92.MirrorCS", {"start": v(-26.34, -74.25) * mm, "end": v(-15, -92.25) * mm});
            skSolve(sketch);
        }
        {
            var Q0;
            Q0=makeQuery(id+"F16.imprint","IMPRINT",FACE,{"disambiguationData":[TD([[makeQuery(id+"F16.imprint","IMPRINT",EDGE,{"derivedFrom":makeQuery(id+"F1.opExtrude","CAP_EDGE",EDGE,{"disambiguationData":[OSD([sQuery(id+"F0.wireOp",EDGE,"E1.left")])],"isStart":true})}),-1.0]])]});
            var Q1;
            Q1=makeQuery(id+"F16.imprint","IMPRINT",FACE,{"disambiguationData":[TD([[makeQuery(id+"F16.imprint","IMPRINT",EDGE,{"derivedFrom":sQuery(id+"F16.wireOp",EDGE,"E80")}),-1.0]])]});
            var Q2;
            Q2=makeQuery(id+"F16.imprint","IMPRINT",FACE,{"disambiguationData":[TD([[makeQuery(id+"F16.imprint","IMPRINT",EDGE,{"derivedFrom":sQuery(id+"F16.wireOp",EDGE,"E87.MirrorCS")}),-1.0]])]});
            var Q3;
            Q3=makeQuery(id+"F2.opExtrude","CAP_FACE",FACE,{"disambiguationData":[OSD([sQuery(id+"F0.wireOp",EDGE,"E12"),sQuery(id+"F0.wireOp",EDGE,"E13"),sQuery(id+"F0.wireOp",EDGE,"E14"),sQuery(id+"F0.wireOp",EDGE,"E15"),sQuery(id+"F0.wireOp",EDGE,"E17.filletArc"),sQuery(id+"F0.wireOp",EDGE,"E18.filletArc"),sQuery(id+"F0.wireOp",EDGE,"E19.filletArc"),sQuery(id+"F0.wireOp",EDGE,"E20.filletArc"),sQuery(id+"F0.wireOp",EDGE,"E25.0"),sQuery(id+"F0.wireOp",EDGE,"E25.1"),sQuery(id+"F0.wireOp",EDGE,"E25.2"),sQuery(id+"F0.wireOp",EDGE,"E25.3"),sQuery(id+"F0.wireOp",EDGE,"E25.4"),sQuery(id+"F0.wireOp",EDGE,"E25.5"),sQuery(id+"F0.wireOp",EDGE,"E25.6"),sQuery(id+"F0.wireOp",EDGE,"E25.7")])],"isStart":false});
            extrude(context, id + "F17", {"entities" : qUnion([Q0, Q1, Q2]), "operationType" : NewBodyOperationType.ADD, "endBound" : BoundingType.UP_TO_SURFACE, "depth" : 25.4 * mm, "endBoundEntityFace" : qUnion([Q3]), "offsetDistance" : 25.4 * mm});
        }
    });
